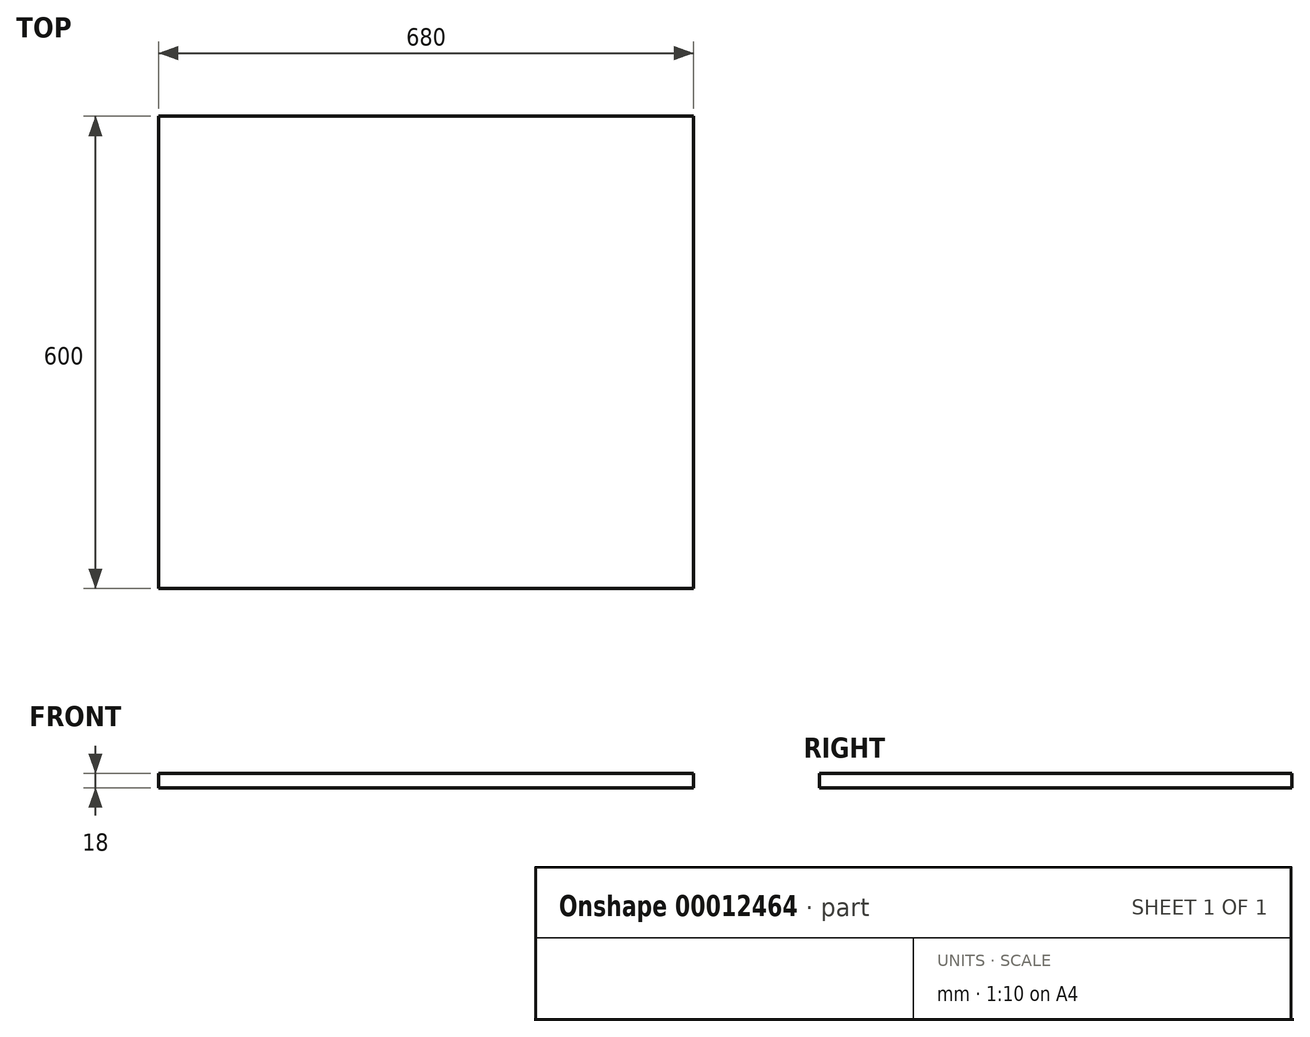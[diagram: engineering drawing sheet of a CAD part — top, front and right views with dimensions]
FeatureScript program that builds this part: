
annotation { "Feature Type Name" : "Feature", "Feature Type Description" : "" }
export const myFeature = defineFeature(function(context is Context, id is Id, definition is map)
    precondition{}
    {
        {
            var Q0;
            Q0=qCreatedBy(makeId("Top.planeOp"),FACE);
            var sketch = newSketch(context, id + "F0", { "sketchPlane" : qUnion([Q0])});
            skLineSegment(sketch, "E0.rect.bottom", {"start": v(340, 300) * mm, "end": v(-340, 300) * mm});
            skLineSegment(sketch, "E0.rect.top", {"start": v(340, -300) * mm, "end": v(-340, -300) * mm});
            skLineSegment(sketch, "E0.rect.left", {"start": v(340, 300) * mm, "end": v(340, -300) * mm});
            skLineSegment(sketch, "E0.rect.right", {"start": v(-340, 300) * mm, "end": v(-340, -300) * mm});
            skPoint(sketch, "E0.rect.middle", {"position": v(0, 0) * mm});
            skSolve(sketch);
        }
        {
            var Q0;
            Q0=makeQuery(id+"F0.imprint","IMPRINT",FACE,{"disambiguationData":[TD([[makeQuery(id+"F0.imprint","IMPRINT",EDGE,{"derivedFrom":sQuery(id+"F0.wireOp",EDGE,"E0.rect.bottom")}),1.0]])]});
            extrude(context, id + "F1", {"entities" : qUnion([Q0]), "depth" : 18 * mm});
        }
    });
